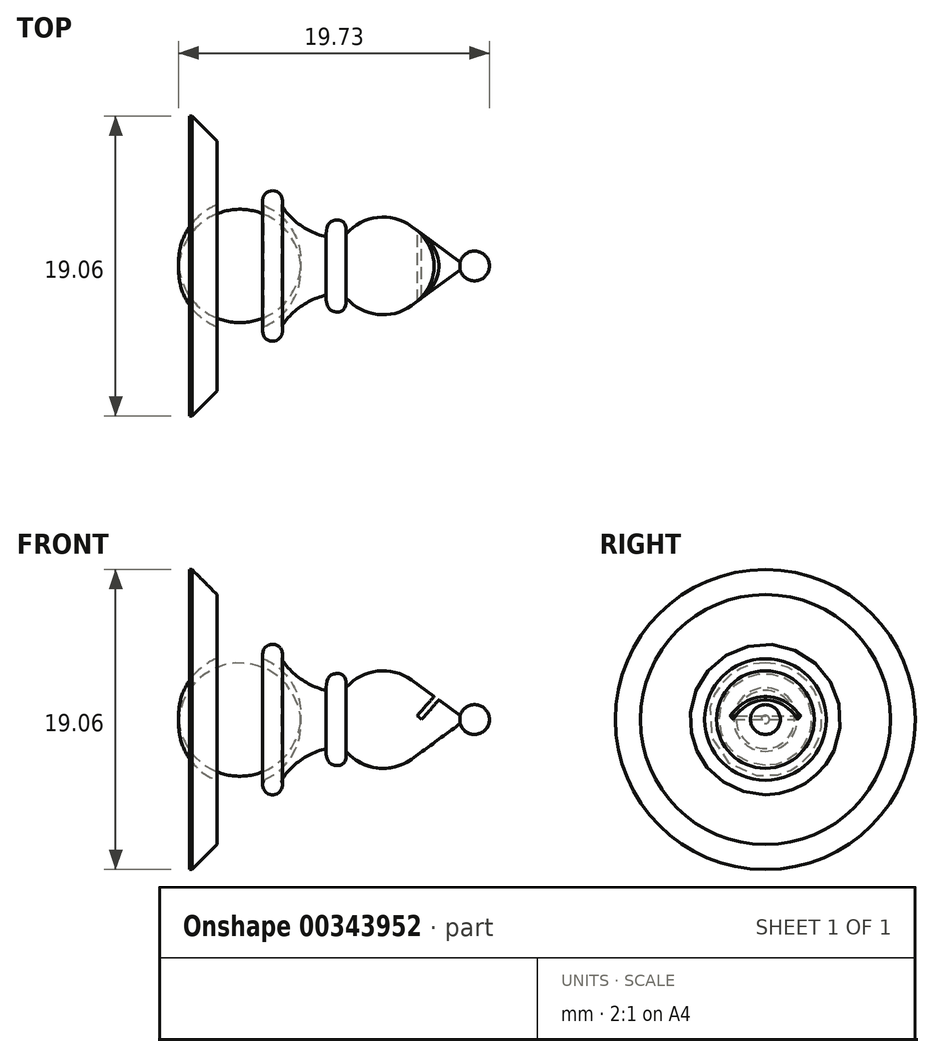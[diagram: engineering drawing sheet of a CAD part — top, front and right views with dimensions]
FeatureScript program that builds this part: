
annotation { "Feature Type Name" : "Feature", "Feature Type Description" : "" }
export const myFeature = defineFeature(function(context is Context, id is Id, definition is map)
    precondition{}
    {
        {
            var Q0;
            Q0=qCreatedBy(makeId("Front.planeOp"),FACE);
            var sketch = newSketch(context, id + "F0", { "sketchPlane" : qUnion([Q0])});
            skLineSegment(sketch, "E0", {"start": v(0, 0) * mm, "end": v(-19.05, 0) * mm});
            skLineSegment(sketch, "E1", {"start": v(-19.05, 0) * mm, "end": v(-19.05, 9.53) * mm});
            skLineSegment(sketch, "E2", {"start": v(-19.05, 9.53) * mm, "end": v(-17.3, 9.53) * mm});
            skLineSegment(sketch, "E3", {"start": v(-17.3, 9.53) * mm, "end": v(-17.3, 3.89) * mm});
            skLineSegment(sketch, "E4", {"start": v(-9.64, 2.92) * mm, "end": v(-9.64, 2.92) * mm});
            skArc(sketch, "E5", {"start": v(0, 0) * mm, "mid": v(-0.82, 0.94) * mm, "end": v(-1.86, 0.26) * mm});
            skArc(sketch, "E6", {"start": v(-4.94, 2.52) * mm, "mid": v(-7.12, 3.08) * mm, "end": v(-9.1, 2.02) * mm});
            skFitSpline(sketch, "E7", {"points": [v(-9.1, 2.02) * mm, v(-9.64, 2.92) * mm, v(-10.36, 1.85) * mm], "startDerivative": vector(0.41, 4.41) * mm, "endDerivative": vector(0.42, -5) * mm});
            skArc(sketch, "E8", {"start": v(-13.2, 3.86) * mm, "mid": v(-13.77, 4.78) * mm, "end": v(-14.34, 3.86) * mm});
            skLineSegment(sketch, "E9", {"start": v(-1.86, 0.26) * mm, "end": v(-4.94, 2.52) * mm});
            skArc(sketch, "E10", {"start": v(-14.34, 3.86) * mm, "mid": v(-15.82, 4.17) * mm, "end": v(-17.3, 3.89) * mm});
            skArc(sketch, "E11", {"start": v(-13.2, 3.86) * mm, "mid": v(-11.98, 2.58) * mm, "end": v(-10.36, 1.85) * mm});
            skSolve(sketch);
        }
        {
            var Q0;
            Q0=makeQuery(id+"F0.imprint","IMPRINT",FACE,{"disambiguationData":[TD([[makeQuery(id+"F0.imprint","IMPRINT",EDGE,{"derivedFrom":sQuery(id+"F0.wireOp",EDGE,"E0")}),-1.0]])]});
            var Q1;
            Q1=sQuery(id+"F0.wireOp",EDGE,"E0");
            revolve(context, id + "F1", {"entities" : qUnion([Q0]), "axis" : qUnion([Q1]), "revolveType" : RevolveType.FULL});
        }
        {
            var Q0;
            Q0=qCreatedBy(makeId("Front.planeOp"),FACE);
            var sketch = newSketch(context, id + "F2", { "sketchPlane" : qUnion([Q0])});
            skLineSegment(sketch, "E12", {"start": v(-3.37, 1.63) * mm, "end": v(-4.58, 0.24) * mm});
            skLineSegment(sketch, "E13", {"start": v(-4.58, 0.24) * mm, "end": v(-4.3, 0) * mm});
            skLineSegment(sketch, "E14", {"start": v(-4.3, 0) * mm, "end": v(-3.05, 1.43) * mm});
            skLineSegment(sketch, "E15", {"start": v(-3.05, 1.43) * mm, "end": v(-3.37, 1.63) * mm});
            skSolve(sketch);
        }
        {
            var Q0;
            Q0=makeQuery(id+"F2.imprint","IMPRINT",FACE,{"disambiguationData":[TD([[makeQuery(id+"F2.imprint","IMPRINT",EDGE,{"derivedFrom":sQuery(id+"F2.wireOp",EDGE,"E12")}),1.0]])]});
            extrude(context, id + "F3", {"entities" : qUnion([Q0]), "operationType" : NewBodyOperationType.REMOVE, "endBound" : BoundingType.SYMMETRIC, "depth" : 25.4 * mm});
        }
        {
            var Q0;
            Q0=makeQuery(id+"F1.opRevolve","SWEPT_EDGE",EDGE,{"disambiguationData":[OSD([sQuery(id+"F0.wireOp",EDGE,"E2"),sQuery(id+"F0.wireOp",EDGE,"E3")])]});
            chamfer(context, id + "F4", {"entities" : qUnion([Q0]), "width" : 1.59 * mm, "tangentPropagation" : true});
        }
    });
